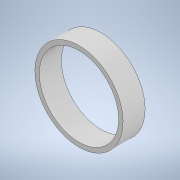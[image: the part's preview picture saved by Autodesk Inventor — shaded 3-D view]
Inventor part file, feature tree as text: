
AUTODESK INVENTOR PART (.ipt)
format: ipt  version: 2020 (Build 240168000, 168)  size: 112,640 bytes
history: native  units: mm
features: other x4, extrude x2, sketch x2, plane x1, reference x1
ambient origin geometry x8: Origin, YZ Plane, XZ Plane, XY Plane, X Axis, Y Axis, Z Axis, Center Point
bodies: 实体1 (feature_tree)
feature tree (10):
  plane  "工作平面1"
  extrude  "拉伸1"  Depth=64.0mm
  extrude  "拉伸2"  Depth=10.0mm
  sketch  "草图1"  dims[d0=80.0mm d1=64.0mm]
  reference  "参考1"
  sketch  "草图2"  dims[d2=20.0mm d3=0.0mm d4=72.0mm d5=10.0mm d6=0.0mm]
  other  "<userpath>\Desktop\ME_course_project\课设试试\shaft_try_1.iam"
  other  "shaft_try_1.iam"
  other  "轴承通盖1:1"
  other  "滚动轴承 GB/T 283 NUP 型 NUP 208 E:2"
